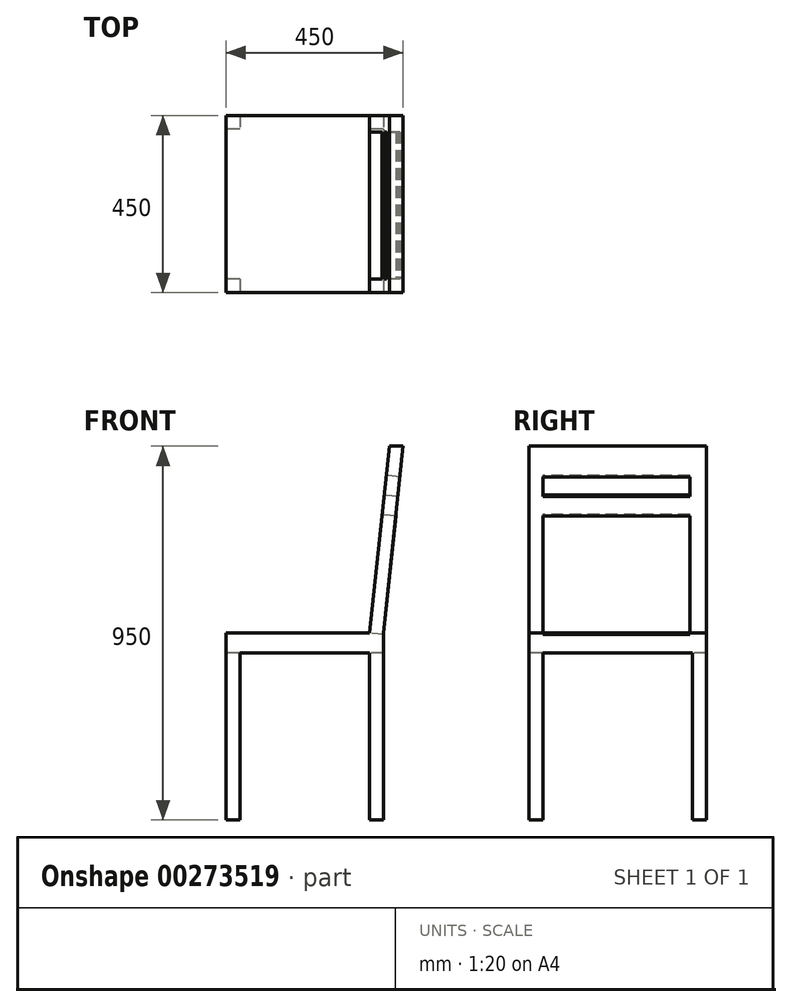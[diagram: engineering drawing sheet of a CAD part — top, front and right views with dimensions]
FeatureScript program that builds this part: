
annotation { "Feature Type Name" : "Feature", "Feature Type Description" : "" }
export const myFeature = defineFeature(function(context is Context, id is Id, definition is map)
    precondition{}
    {
        {
            var Q0;
            Q0=qCreatedBy(makeId("Top.planeOp"),FACE);
            var sketch = newSketch(context, id + "F0", { "sketchPlane" : qUnion([Q0])});
            skLineSegment(sketch, "E0.bottom", {"start": v(225, 225) * mm, "end": v(-225, 225) * mm});
            skLineSegment(sketch, "E0.top", {"start": v(225, -225) * mm, "end": v(-225, -225) * mm});
            skLineSegment(sketch, "E0.left", {"start": v(225, 225) * mm, "end": v(225, -225) * mm});
            skLineSegment(sketch, "E0.right", {"start": v(-225, 225) * mm, "end": v(-225, -225) * mm});
            skPoint(sketch, "E0.middle", {"position": v(0, 0) * mm});
            skSolve(sketch);
        }
        {
            var Q0;
            Q0=qSketchRegion(id+"F0",true);
            extrude(context, id + "F1", {"entities" : qUnion([Q0]), "depth" : 950 * mm});
        }
        {
            var Q0;
            Q0=makeQuery(id+"F1.opExtrude","SWEPT_FACE",FACE,{"disambiguationData":[OSD([sQuery(id+"F0.wireOp",EDGE,"E0.top")])]});
            var sketch = newSketch(context, id + "F2", { "sketchPlane" : qUnion([Q0])});
            skLineSegment(sketch, "E1.bottom", {"start": v(225, 475) * mm, "end": v(-225, 475) * mm});
            skLineSegment(sketch, "E1.top", {"start": v(225, 425) * mm, "end": v(-225, 425) * mm});
            skLineSegment(sketch, "E1.left", {"start": v(225, 475) * mm, "end": v(225, 425) * mm});
            skLineSegment(sketch, "E1.right", {"start": v(-225, 475) * mm, "end": v(-225, 425) * mm});
            skLineSegment(sketch, "E2", {"start": v(225, 950) * mm, "end": v(175, 475) * mm});
            skLineSegment(sketch, "E3", {"start": v(190, 950) * mm, "end": v(140, 475) * mm});
            skLineSegment(sketch, "E4", {"start": v(175, 475) * mm, "end": v(175, 0) * mm});
            skLineSegment(sketch, "E5", {"start": v(140, 475) * mm, "end": v(140, 0) * mm});
            skLineSegment(sketch, "E6.bottom", {"start": v(-225, 425) * mm, "end": v(-190, 425) * mm});
            skLineSegment(sketch, "E6.top", {"start": v(-225, 425) * mm, "end": v(-190, 425) * mm});
            skLineSegment(sketch, "E6.left", {"start": v(-225, 425) * mm, "end": v(-225, 425) * mm});
            skLineSegment(sketch, "E6.right", {"start": v(-190, 425) * mm, "end": v(-190, 425) * mm});
            skLineSegment(sketch, "E7.bottom", {"start": v(-190, 0) * mm, "end": v(-225, 0) * mm});
            skLineSegment(sketch, "E7.top", {"start": v(-190, 425) * mm, "end": v(-225, 425) * mm});
            skLineSegment(sketch, "E7.left", {"start": v(-190, 0) * mm, "end": v(-190, 425) * mm});
            skLineSegment(sketch, "E7.right", {"start": v(-225, 0) * mm, "end": v(-225, 425) * mm});
            skSolve(sketch);
        }
        {
            var Q0;
            {var subQ0=sQuery(id+"F2.wireOp",EDGE,"E1.left");Q0=makeQuery(id+"F2.imprint","IMPRINT",FACE,{"disambiguationData":[TD([[makeQuery(id+"F2.imprint","IMPRINT",EDGE,{"derivedFrom":subQ0}),-1.0]])]});}
            var Q1;
            {var subQ4=sQuery(id+"F2.wireOp",EDGE,"E3");Q1=makeQuery(id+"F2.imprint","IMPRINT",FACE,{"disambiguationData":[TD([[makeQuery(id+"F2.imprint","IMPRINT",EDGE,{"derivedFrom":subQ4}),-1.0]])]});}
            var Q2;
            {var subQ4=sQuery(id+"F2.wireOp",EDGE,"E2");Q2=makeQuery(id+"F2.imprint","IMPRINT",FACE,{"disambiguationData":[TD([[makeQuery(id+"F2.imprint","IMPRINT",EDGE,{"derivedFrom":subQ4}),1.0]])]});}
            var Q3;
            {var subQ0=sQuery(id+"F2.wireOp",EDGE,"E7.left");Q3=makeQuery(id+"F2.imprint","IMPRINT",FACE,{"disambiguationData":[TD([[makeQuery(id+"F2.imprint","IMPRINT",EDGE,{"derivedFrom":subQ0}),-1.0]])]});}
            var Q4;
            {var subQ1=sQuery(id+"F0.wireOp",EDGE,"E0.top");var subQ4=sQuery(id+"F2.wireOp",EDGE,"E4");var subQ6=makeQuery(id+"F1.opExtrude","CAP_EDGE",EDGE,{"disambiguationData":[OSD([subQ1])],"isStart":true});var subQ7=makeQuery(id+"F2.imprint","INTERSECT",VERTEX,{"derivedFrom":[subQ6,subQ4]});Q4=makeQuery(id+"F2.imprint","IMPRINT",FACE,{"disambiguationData":[TD([[makeQuery(id+"F2.imprint","IMPRINT",EDGE,{"disambiguationData":[TD([[subQ7,1.0]])],"derivedFrom":subQ4}),1.0]])]});}
            extrude(context, id + "F3", {"entities" : qUnion([Q0, Q1, Q2, Q3, Q4]), "operationType" : NewBodyOperationType.REMOVE, "endBound" : BoundingType.THROUGH_ALL, "oppositeDirection" : true, "depth" : 25 * mm});
        }
        {
            var Q0;
            Q0=makeQuery(id+"F1.opExtrude","SWEPT_FACE",FACE,{"disambiguationData":[OSD([sQuery(id+"F0.wireOp",EDGE,"E0.right")])]});
            var sketch = newSketch(context, id + "F4", { "sketchPlane" : qUnion([Q0])});
            skLineSegment(sketch, "E8", {"start": v(-190, 0) * mm, "end": v(-190, 425) * mm});
            skLineSegment(sketch, "E9", {"start": v(-190, 425) * mm, "end": v(190, 425) * mm});
            skLineSegment(sketch, "E10", {"start": v(190, 425) * mm, "end": v(190, 0) * mm});
            skSolve(sketch);
        }
        {
            var Q0;
            Q0 = qSketchRegion(id + "F4", true);
            var Q1;
            {var subQ0=sQuery(id+"F4.wireOp",EDGE,"E8");Q1=makeQuery(id+"F4.imprint","IMPRINT",FACE,{"disambiguationData":[TD([[makeQuery(id+"F4.imprint","IMPRINT",EDGE,{"derivedFrom":subQ0}),-1.0]])]});}
            extrude(context, id + "F5", {"entities" : qUnion([Q0, Q1]), "operationType" : NewBodyOperationType.REMOVE, "endBound" : BoundingType.THROUGH_ALL, "oppositeDirection" : true, "depth" : 25 * mm});
        }
        {
            var Q0;
            Q0=makeQuery(id+"F3.boolean.opBoolean","COPY",FACE,{"derivedFrom":makeQuery(id+"F3.opExtrude","SWEPT_FACE",FACE,{"disambiguationData":[OSD([sQuery(id+"F2.wireOp",EDGE,"E3")])]})});
            var sketch = newSketch(context, id + "F6", { "sketchPlane" : qUnion([Q0])});
            skLineSegment(sketch, "E11", {"start": v(-183.3, 487.05) * mm, "end": v(-183.3, 889.67) * mm});
            skLineSegment(sketch, "E12", {"start": v(-183.3, 889.67) * mm, "end": v(190, 889.67) * mm});
            skLineSegment(sketch, "E13", {"start": v(190, 889.67) * mm, "end": v(190, 487.05) * mm});
            skLineSegment(sketch, "E14", {"start": v(-183.3, 839.67) * mm, "end": v(190, 839.67) * mm});
            skLineSegment(sketch, "E15", {"start": v(-183.3, 789.67) * mm, "end": v(190, 789.67) * mm});
            skSolve(sketch);
        }
        {
            var Q0;
            {var subQ0=sQuery(id+"F6.wireOp",EDGE,"E12");Q0=makeQuery(id+"F6.imprint","IMPRINT",FACE,{"disambiguationData":[TD([[makeQuery(id+"F6.imprint","IMPRINT",EDGE,{"derivedFrom":subQ0}),-1.0]])]});}
            var Q1;
            {var subQ3=sQuery(id+"F6.wireOp",EDGE,"E15");Q1=makeQuery(id+"F6.imprint","IMPRINT",FACE,{"disambiguationData":[TD([[makeQuery(id+"F6.imprint","IMPRINT",EDGE,{"derivedFrom":subQ3}),-1.0]])]});}
            extrude(context, id + "F7", {"entities" : qUnion([Q0, Q1]), "operationType" : NewBodyOperationType.REMOVE, "endBound" : BoundingType.THROUGH_ALL, "oppositeDirection" : true, "depth" : 25 * mm});
        }
    });
